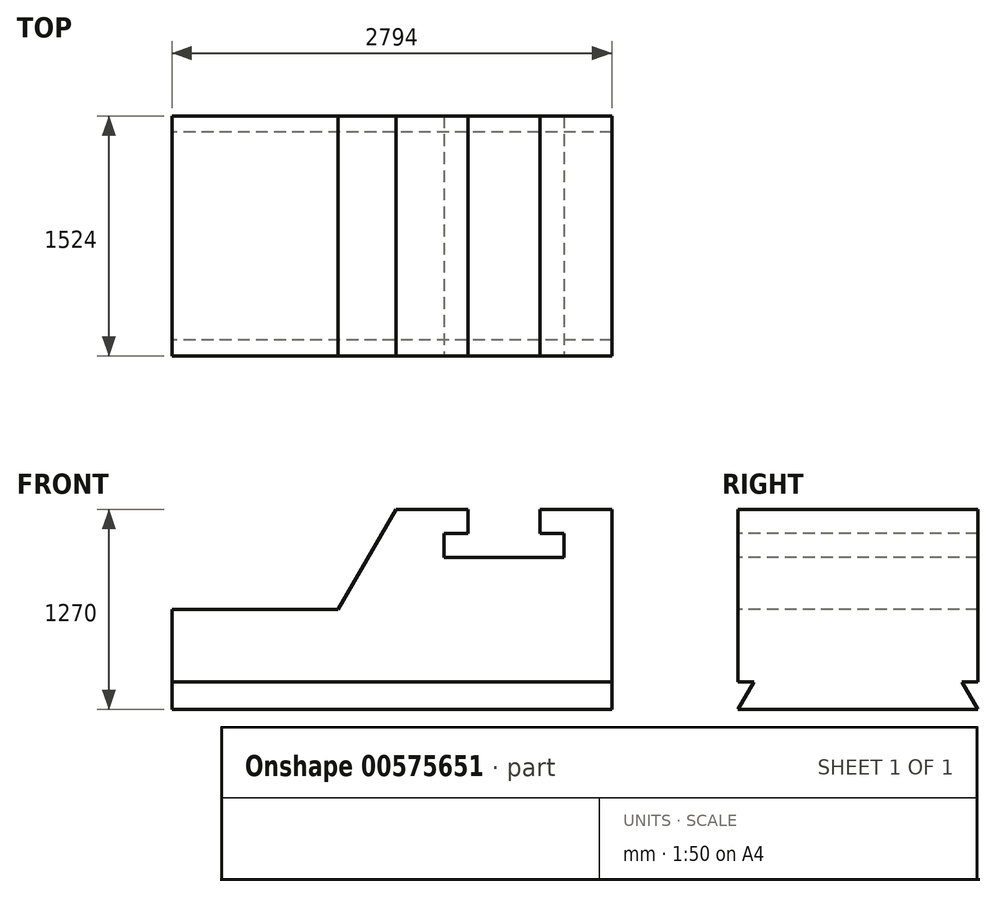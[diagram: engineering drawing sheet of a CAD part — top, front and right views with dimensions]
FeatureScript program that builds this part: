
annotation { "Feature Type Name" : "Feature", "Feature Type Description" : "" }
export const myFeature = defineFeature(function(context is Context, id is Id, definition is map)
    precondition{}
    {
        {
            var Q0;
            Q0=qCreatedBy(makeId("Front.planeOp"),FACE);
            var sketch = newSketch(context, id + "F0", { "sketchPlane" : qUnion([Q0])});
            skLineSegment(sketch, "E0.bottom", {"start": v(0, 0) * mm, "end": v(-2794, 0) * mm});
            skLineSegment(sketch, "E0.top", {"start": v(0, 1270) * mm, "end": v(-2794, 1270) * mm});
            skLineSegment(sketch, "E0.left", {"start": v(0, 0) * mm, "end": v(0, 1270) * mm});
            skLineSegment(sketch, "E0.right", {"start": v(-2794, 0) * mm, "end": v(-2794, 1270) * mm});
            skSolve(sketch);
        }
        {
            var Q0;
            Q0=makeQuery(id+"F0.imprint","IMPRINT",FACE,{"disambiguationData":[TD([[makeQuery(id+"F0.imprint","IMPRINT",EDGE,{"derivedFrom":sQuery(id+"F0.wireOp",EDGE,"E0.bottom")}),-1.0]])]});
            var Q1;
            Q1 = qSketchRegion(id + "F0", true);
            extrude(context, id + "F1", {"entities" : qUnion([Q0, Q1]), "depth" : 1524 * mm, "offsetDistance" : 25.4 * mm});
        }
        {
            var Q0;
            Q0=makeQuery(id+"F1.opExtrude","CAP_FACE",FACE,{"disambiguationData":[OSD([sQuery(id+"F0.wireOp",EDGE,"E0.bottom"),sQuery(id+"F0.wireOp",EDGE,"E0.top"),sQuery(id+"F0.wireOp",EDGE,"E0.left"),sQuery(id+"F0.wireOp",EDGE,"E0.right")])],"isStart":false});
            var sketch = newSketch(context, id + "F2", { "sketchPlane" : qUnion([Q0])});
            skLineSegment(sketch, "E1", {"start": v(0, 1270) * mm, "end": v(0, 965.2) * mm});
            skLineSegment(sketch, "E2", {"start": v(0, 965.2) * mm, "end": v(-304.8, 965.2) * mm});
            skLineSegment(sketch, "E3.bottom", {"start": v(-304.8, 965.2) * mm, "end": v(-1066.8, 965.2) * mm});
            skLineSegment(sketch, "E3.top", {"start": v(-304.8, 1117.6) * mm, "end": v(-1066.8, 1117.6) * mm});
            skLineSegment(sketch, "E3.left", {"start": v(-304.8, 965.2) * mm, "end": v(-304.8, 1117.6) * mm});
            skLineSegment(sketch, "E3.right", {"start": v(-1066.8, 965.2) * mm, "end": v(-1066.8, 1117.6) * mm});
            skLineSegment(sketch, "E4.bottom", {"start": v(-304.8, 1117.6) * mm, "end": v(-457.2, 1117.6) * mm});
            skLineSegment(sketch, "E4.top", {"start": v(-304.8, 1117.6) * mm, "end": v(-457.2, 1117.6) * mm});
            skLineSegment(sketch, "E4.left", {"start": v(-304.8, 1117.6) * mm, "end": v(-304.8, 1117.6) * mm});
            skLineSegment(sketch, "E4.right", {"start": v(-457.2, 1117.6) * mm, "end": v(-457.2, 1117.6) * mm});
            skLineSegment(sketch, "E5.bottom", {"start": v(-457.2, 1117.6) * mm, "end": v(-914.4, 1117.6) * mm});
            skLineSegment(sketch, "E5.top", {"start": v(-457.2, 1270) * mm, "end": v(-914.4, 1270) * mm});
            skLineSegment(sketch, "E5.left", {"start": v(-457.2, 1117.6) * mm, "end": v(-457.2, 1270) * mm});
            skLineSegment(sketch, "E5.right", {"start": v(-914.4, 1117.6) * mm, "end": v(-914.4, 1270) * mm});
            skSolve(sketch);
        }
        {
            var Q0;
            Q0 = qSketchRegion(id + "F2", true);
            extrude(context, id + "F3", {"entities" : qUnion([Q0]), "operationType" : NewBodyOperationType.REMOVE, "endBound" : BoundingType.THROUGH_ALL, "oppositeDirection" : true, "depth" : 25.4 * mm, "offsetDistance" : 25.4 * mm});
        }
        {
            var Q0;
            Q0=makeQuery(id+"F1.opExtrude","CAP_FACE",FACE,{"disambiguationData":[OSD([sQuery(id+"F0.wireOp",EDGE,"E0.bottom"),sQuery(id+"F0.wireOp",EDGE,"E0.top"),sQuery(id+"F0.wireOp",EDGE,"E0.left"),sQuery(id+"F0.wireOp",EDGE,"E0.right")])],"isStart":false});
            var sketch = newSketch(context, id + "F4", { "sketchPlane" : qUnion([Q0])});
            skLineSegment(sketch, "E6", {"start": v(-914.4, 1270) * mm, "end": v(-1371.6, 1270) * mm});
            skLineSegment(sketch, "E7", {"start": v(-2794, 0) * mm, "end": v(-2794, 635) * mm});
            skLineSegment(sketch, "E8", {"start": v(-2794, 635) * mm, "end": v(-1738.22, 635) * mm});
            skLineSegment(sketch, "E9", {"start": v(-1371.6, 1270) * mm, "end": v(-1738.22, 635) * mm});
            skSolve(sketch);
        }
        {
            var Q0;
            {var subQ0=sQuery(id+"F4.wireOp",EDGE,"E8");Q0=makeQuery(id+"F4.imprint","IMPRINT",FACE,{"disambiguationData":[TD([[makeQuery(id+"F4.imprint","IMPRINT",EDGE,{"derivedFrom":subQ0}),1.0]])]});}
            extrude(context, id + "F5", {"entities" : qUnion([Q0]), "operationType" : NewBodyOperationType.REMOVE, "endBound" : BoundingType.THROUGH_ALL, "oppositeDirection" : true, "depth" : 25.4 * mm, "offsetDistance" : 25.4 * mm});
        }
        {
            var Q0;
            Q0=makeQuery(id+"F1.opExtrude","SWEPT_FACE",FACE,{"disambiguationData":[OSD([sQuery(id+"F0.wireOp",EDGE,"E0.right")])]});
            var sketch = newSketch(context, id + "F6", { "sketchPlane" : qUnion([Q0])});
            skLineSegment(sketch, "E10", {"start": v(0, 0) * mm, "end": v(101.6, 175.98) * mm});
            skLineSegment(sketch, "E11", {"start": v(1524, 0) * mm, "end": v(1422.4, 175.98) * mm});
            skLineSegment(sketch, "E12", {"start": v(101.6, 175.98) * mm, "end": v(0, 175.98) * mm});
            skLineSegment(sketch, "E13", {"start": v(1422.4, 175.98) * mm, "end": v(1524, 175.98) * mm});
            skSolve(sketch);
        }
        {
            var Q0;
            {var subQ0=sQuery(id+"F6.wireOp",EDGE,"E10");Q0=makeQuery(id+"F6.imprint","IMPRINT",FACE,{"disambiguationData":[TD([[makeQuery(id+"F6.imprint","IMPRINT",EDGE,{"derivedFrom":subQ0}),1.0]])]});}
            var Q1;
            {var subQ0=sQuery(id+"F6.wireOp",EDGE,"E11");Q1=makeQuery(id+"F6.imprint","IMPRINT",FACE,{"disambiguationData":[TD([[makeQuery(id+"F6.imprint","IMPRINT",EDGE,{"derivedFrom":subQ0}),-1.0]])]});}
            extrude(context, id + "F7", {"entities" : qUnion([Q0, Q1]), "operationType" : NewBodyOperationType.REMOVE, "endBound" : BoundingType.THROUGH_ALL, "oppositeDirection" : true, "depth" : 25.4 * mm, "offsetDistance" : 25.4 * mm});
        }
    });
